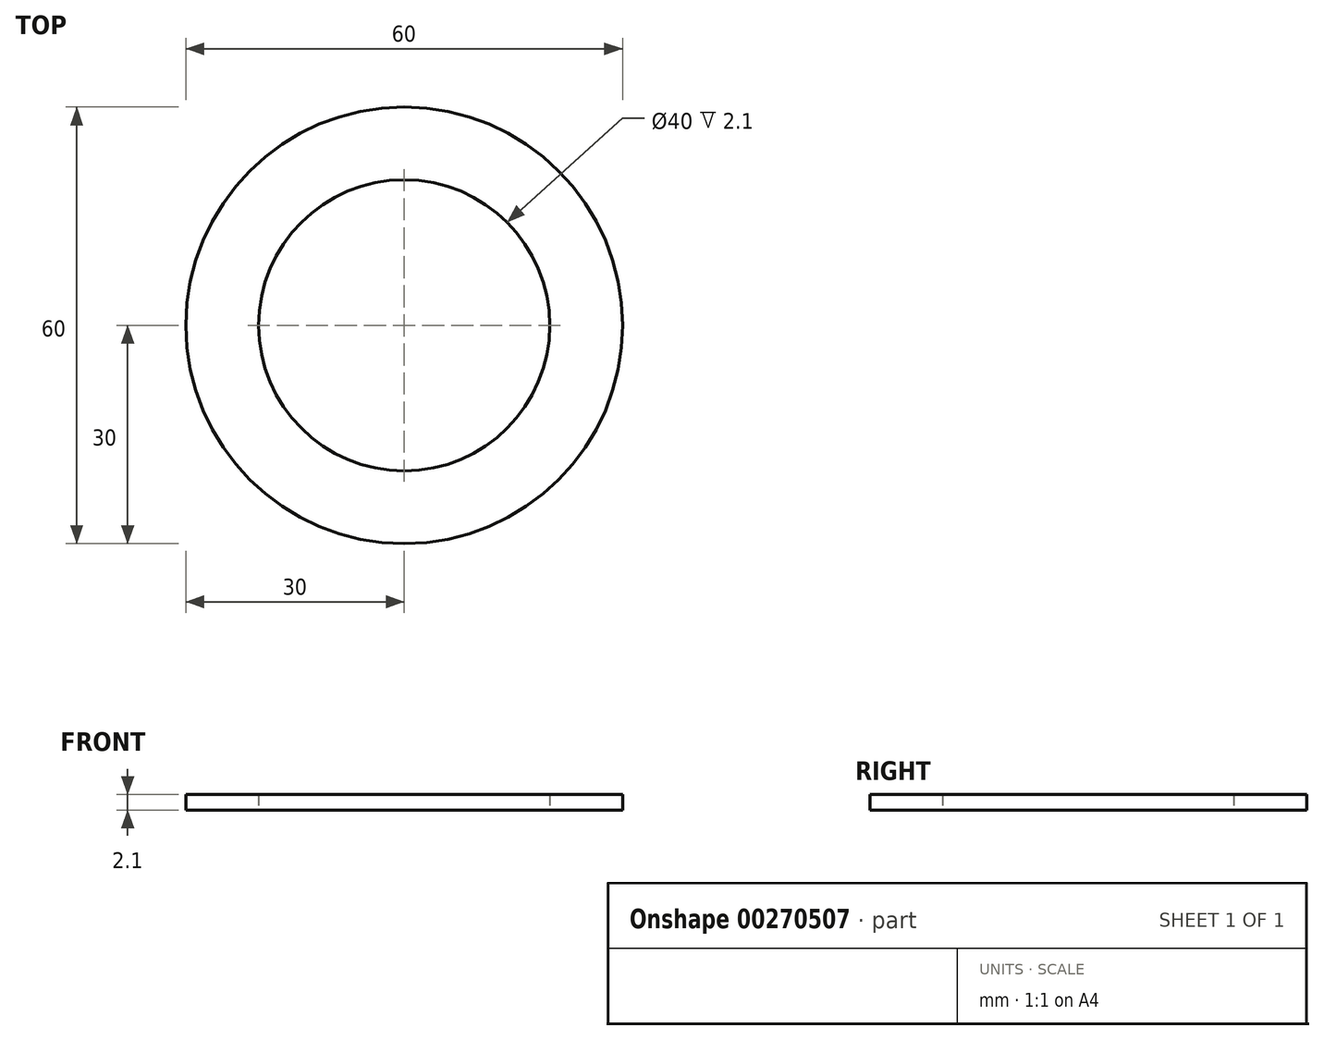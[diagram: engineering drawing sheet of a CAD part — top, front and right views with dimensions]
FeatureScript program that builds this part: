
annotation { "Feature Type Name" : "Feature", "Feature Type Description" : "" }
export const myFeature = defineFeature(function(context is Context, id is Id, definition is map)
    precondition{}
    {
        {
            var Q0;
            Q0=qCreatedBy(makeId("Top.planeOp"),FACE);
            var sketch = newSketch(context, id + "F0", { "sketchPlane" : qUnion([Q0])});
            skCircle(sketch, "E0", {"center": v(0, 0) * mm, "radius": 20 * mm});
            skCircle(sketch, "E1", {"center": v(0, 0) * mm, "radius": 30 * mm});
            skSolve(sketch);
        }
        {
            var Q0;
            Q0 = qSketchRegion(id + "F0", true);
            extrude(context, id + "F1", {"entities" : qUnion([Q0]), "depth" : 2.1 * mm});
        }
    });
